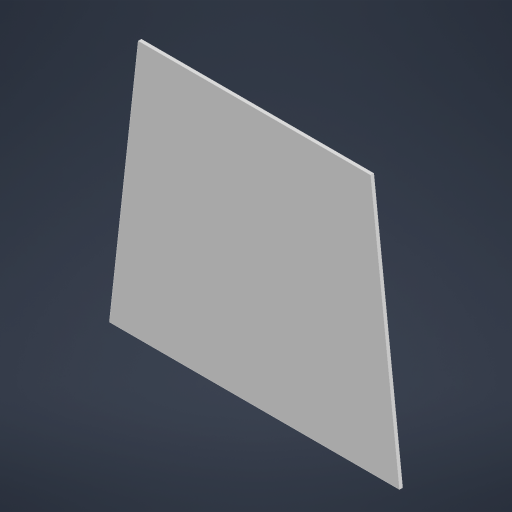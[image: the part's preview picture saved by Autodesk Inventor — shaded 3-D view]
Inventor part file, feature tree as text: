
AUTODESK INVENTOR PART (.ipt)
format: ipt  version: 2023.2 (Build 272271000, 271)  size: 281,600 bytes
history: native  units: mm
features: sketch x2
ambient origin geometry x8: Origin, YZ Plane, XZ Plane, XY Plane, X Axis, Y Axis, Z Axis, Center Point
bodies: Body1 (feature_tree)
feature tree (2):
  sketch  "Sketch1"  dims[d229=90.0mm]
  sketch  "Sketch2"  dims[d232=16.0mm d233=12.0mm d234=12.0mm d235=4.0mm d237=4.0mm d238=0.0mm d239=14.0mm d241=130.0mm d242=100.0mm d243=17.0mm d245=8.0mm d246=10.0mm d247=80.0mm d249=10.0mm d250=4.0mm d251=0.0mm d256=2.5mm d257=0.0mm d258=1.5mm d259=0.0mm d260=2.5mm d261=0.0mm d9=0.5mm d10=0.872665mm d11=0.5mm d12=0.872665mm d13=0.5mm d14=0.872665mm d27=0.5mm d28=0.872665mm d29=0.5mm d30=0.872665mm d88=0.5mm d89=0.872665mm d90=0.5mm d91=0.872665mm d116=0.5mm d117=0.872665mm d118=0.5mm d119=0.872665mm d154=0.5mm d155=0.872665mm d156=0.5mm d157=0.872665mm d181=0.5mm d182=0.872665mm d183=0.5mm d184=0.872665mm d221=0.5mm d222=0.872665mm d223=0.5mm d224=0.872665mm d262=0.5mm d263=0.872665mm]
